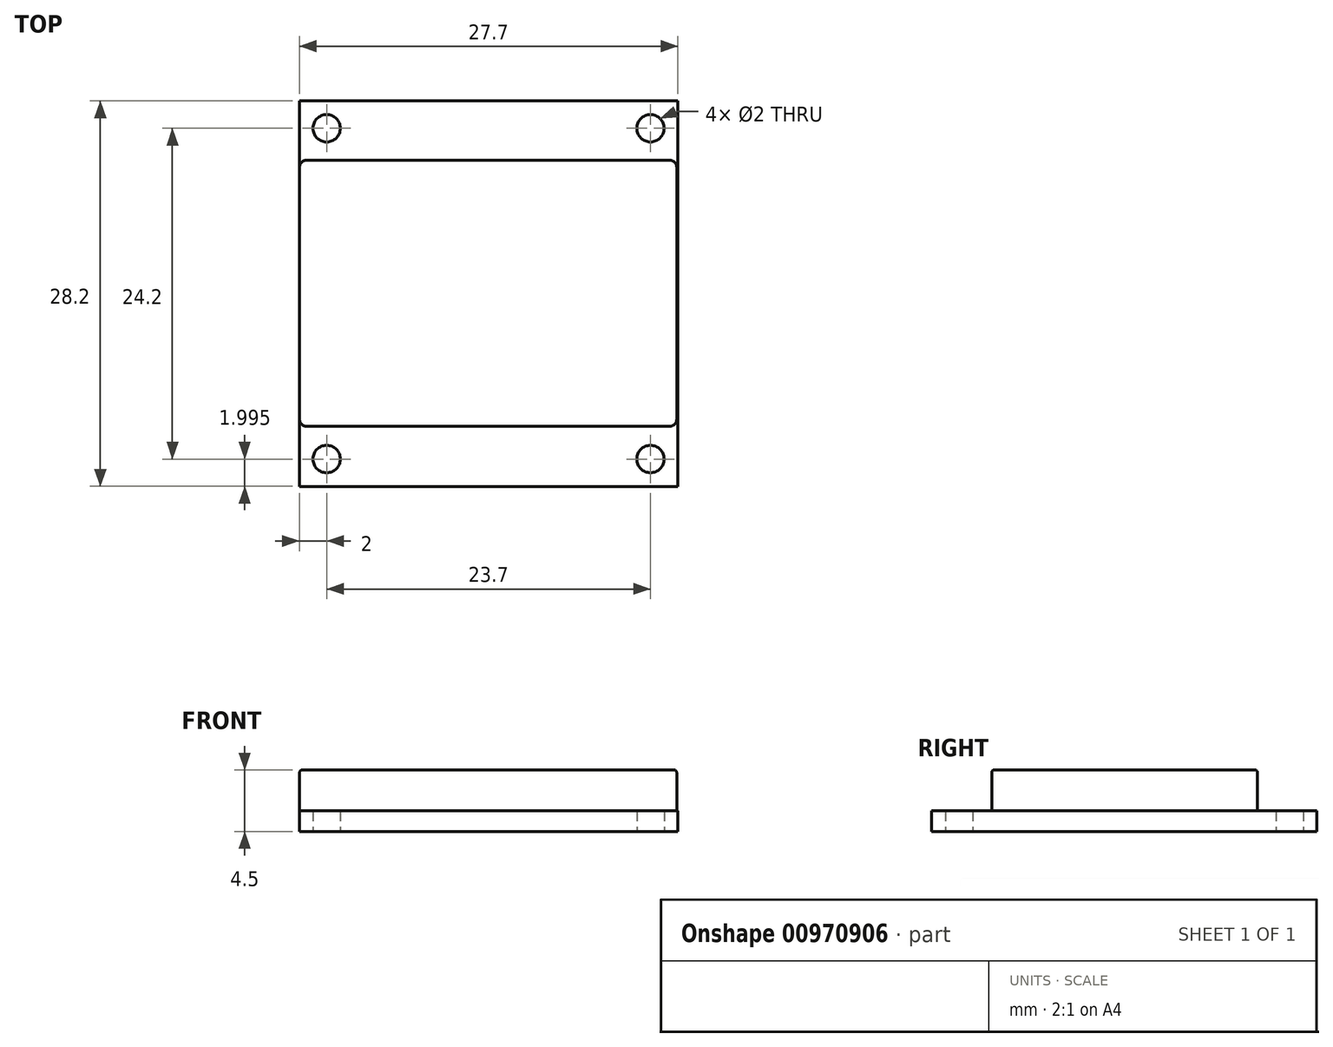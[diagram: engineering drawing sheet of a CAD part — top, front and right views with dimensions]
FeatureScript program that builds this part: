
annotation { "Feature Type Name" : "Feature", "Feature Type Description" : "" }
export const myFeature = defineFeature(function(context is Context, id is Id, definition is map)
    precondition{}
    {
        {
            var Q0;
            Q0=qCreatedBy(makeId("Top.planeOp"),FACE);
            var sketch = newSketch(context, id + "F0", { "sketchPlane" : qUnion([Q0])});
            skLineSegment(sketch, "E0.bottom", {"start": v(-13.82, 14.08) * mm, "end": v(13.88, 14.08) * mm});
            skLineSegment(sketch, "E0.top", {"start": v(-13.82, -14.12) * mm, "end": v(13.88, -14.12) * mm});
            skLineSegment(sketch, "E0.left", {"start": v(-13.82, 14.08) * mm, "end": v(-13.82, -14.12) * mm});
            skLineSegment(sketch, "E0.right", {"start": v(13.88, 14.08) * mm, "end": v(13.88, -14.12) * mm});
            skLineSegment(sketch, "E1", {"start": v(0.03, 14.08) * mm, "end": v(0.03, -14.12) * mm, "construction": true});
            skLineSegment(sketch, "E2", {"start": v(13.88, -0.02) * mm, "end": v(-13.82, -0.02) * mm, "construction": true});
            skCircle(sketch, "E3", {"center": v(11.88, 12.08) * mm, "radius": 1 * mm});
            skCircle(sketch, "E4", {"center": v(11.88, -12.12) * mm, "radius": 1 * mm});
            skCircle(sketch, "E5", {"center": v(-11.82, -12.12) * mm, "radius": 1 * mm});
            skCircle(sketch, "E6", {"center": v(-11.82, 12.08) * mm, "radius": 1 * mm});
            skSolve(sketch);
        }
        {
            assignVariable(context, id + "F1", {"name" : "spessore_pcb", "anyValue" : 1.5 * mm});
        }
        {
            var Q0;
            Q0 = qSketchRegion(id + "F0", true);
            extrude(context, id + "F2", {"entities" : qUnion([Q0]), "depth" : getVariable(context, 'spessore_pcb'), "offsetDistance" : 25 * mm});
        }
        {
            var Q0;
            Q0=makeQuery(id+"F2.opExtrude","CAP_FACE",FACE,{"disambiguationData":[OSD([sQuery(id+"F0.wireOp",EDGE,"E0.bottom"),sQuery(id+"F0.wireOp",EDGE,"E0.top"),sQuery(id+"F0.wireOp",EDGE,"E0.left"),sQuery(id+"F0.wireOp",EDGE,"E0.right"),sQuery(id+"F0.wireOp",EDGE,"E3"),sQuery(id+"F0.wireOp",EDGE,"E4"),sQuery(id+"F0.wireOp",EDGE,"E5"),sQuery(id+"F0.wireOp",EDGE,"E6")])],"isStart":false});
            var sketch = newSketch(context, id + "F3", { "sketchPlane" : qUnion([Q0])});
            skLineSegment(sketch, "E7.bottom", {"start": v(-13.8, 9.73) * mm, "end": v(13.8, 9.73) * mm});
            skLineSegment(sketch, "E7.top", {"start": v(-13.8, -9.73) * mm, "end": v(13.8, -9.73) * mm});
            skLineSegment(sketch, "E7.left", {"start": v(-13.8, 9.73) * mm, "end": v(-13.8, -9.73) * mm});
            skLineSegment(sketch, "E7.right", {"start": v(13.8, 9.73) * mm, "end": v(13.8, -9.73) * mm});
            skSolve(sketch);
        }
        {
            var Q0;
            Q0=makeQuery(id+"F3.imprint","IMPRINT",FACE,{"disambiguationData":[TD([[makeQuery(id+"F3.imprint","IMPRINT",EDGE,{"derivedFrom":sQuery(id+"F3.wireOp",EDGE,"E7.bottom")}),-1.0]])]});
            extrude(context, id + "F4", {"entities" : qUnion([Q0]), "operationType" : NewBodyOperationType.ADD, "depth" : 3 * mm, "offsetDistance" : 25 * mm});
        }
        {
            var Q0;
            Q0=makeQuery(id+"F4.opExtrude","SWEPT_EDGE",EDGE,{"disambiguationData":[OSD([sQuery(id+"F3.wireOp",EDGE,"E7.top"),sQuery(id+"F3.wireOp",EDGE,"E7.right")])]});
            var Q1;
            Q1=makeQuery(id+"F4.opExtrude","SWEPT_EDGE",EDGE,{"disambiguationData":[OSD([sQuery(id+"F3.wireOp",EDGE,"E7.bottom"),sQuery(id+"F3.wireOp",EDGE,"E7.right")])]});
            var Q2;
            Q2=makeQuery(id+"F4.opExtrude","SWEPT_EDGE",EDGE,{"disambiguationData":[OSD([sQuery(id+"F3.wireOp",EDGE,"E7.bottom"),sQuery(id+"F3.wireOp",EDGE,"E7.left")])]});
            var Q3;
            Q3=makeQuery(id+"F4.opExtrude","SWEPT_EDGE",EDGE,{"disambiguationData":[OSD([sQuery(id+"F3.wireOp",EDGE,"E7.top"),sQuery(id+"F3.wireOp",EDGE,"E7.left")])]});
            fillet(context, id + "F5", {"entities" : qUnion([Q0, Q1, Q2, Q3]), "radius" : 0.5 * mm, "tangentPropagation" : true, "allowEdgeOverflow" : false});
        }
        {
            var Q0;
            Q0=makeQuery(id+"F4.opExtrude","CAP_FACE",FACE,{"disambiguationData":[OSD([sQuery(id+"F3.wireOp",EDGE,"E7.bottom"),sQuery(id+"F3.wireOp",EDGE,"E7.top"),sQuery(id+"F3.wireOp",EDGE,"E7.left"),sQuery(id+"F3.wireOp",EDGE,"E7.right")])],"isStart":false});
            fillet(context, id + "F6", {"entities" : qUnion([Q0]), "radius" : 0.2 * mm, "tangentPropagation" : true, "allowEdgeOverflow" : false});
        }
    });
